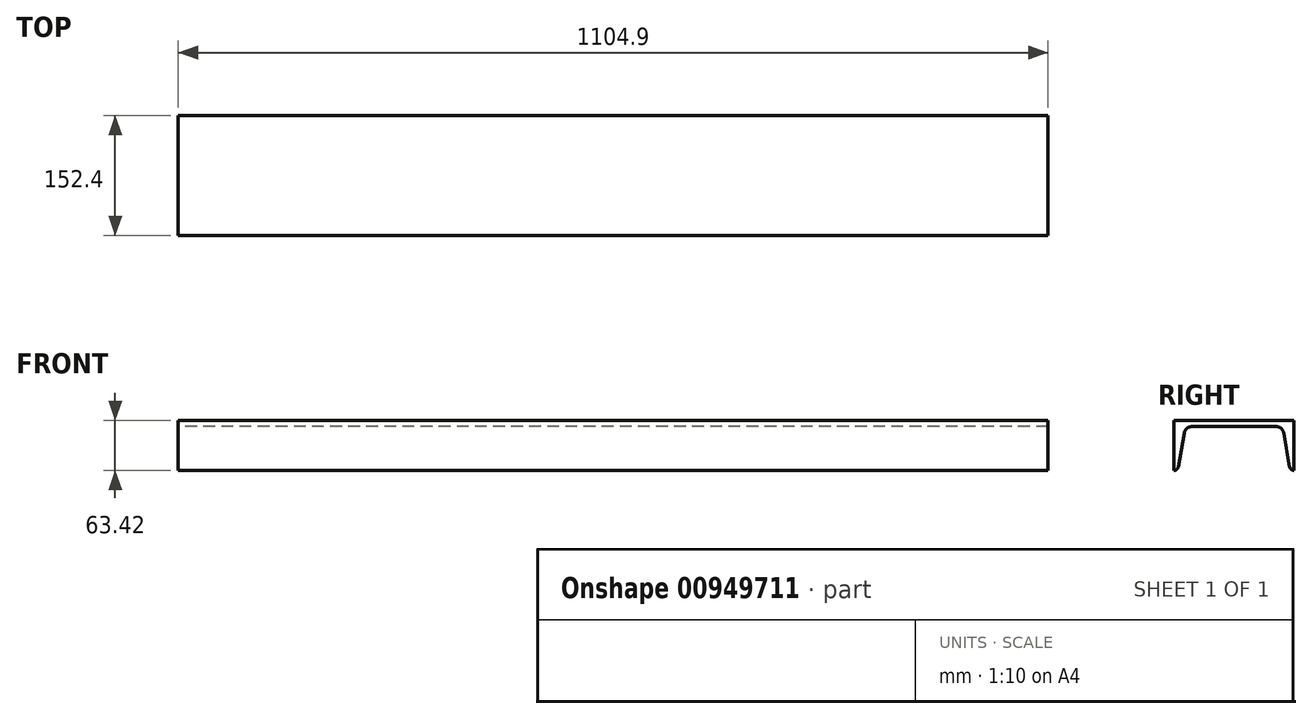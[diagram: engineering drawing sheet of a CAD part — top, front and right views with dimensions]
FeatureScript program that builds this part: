
annotation { "Feature Type Name" : "Feature", "Feature Type Description" : "" }
export const myFeature = defineFeature(function(context is Context, id is Id, definition is map)
    precondition{}
    {
        {
            var Q0;
            Q0=qCreatedBy(makeId("Right.planeOp"),FACE);
            var sketch = newSketch(context, id + "F0", { "sketchPlane" : qUnion([Q0])});
            skLineSegment(sketch, "E0", {"start": v(-76.2, 0) * mm, "end": v(76.2, 0) * mm});
            skLineSegment(sketch, "E1", {"start": v(76.2, 0) * mm, "end": v(76.2, -63.42) * mm});
            skLineSegment(sketch, "E2", {"start": v(-76.2, 0) * mm, "end": v(-76.2, -63.42) * mm});
            skLineSegment(sketch, "E3", {"start": v(-63.12, -15.57) * mm, "end": v(-70.65, -58.76) * mm});
            skLineSegment(sketch, "E4", {"start": v(63.12, -15.57) * mm, "end": v(70.65, -58.76) * mm});
            skLineSegment(sketch, "E5", {"start": v(-53.98, -7.87) * mm, "end": v(53.98, -7.87) * mm});
            skArc(sketch, "E6.filletArc", {"start": v(-76.2, -63.42) * mm, "mid": v(-72.57, -62.1) * mm, "end": v(-70.65, -58.76) * mm});
            skArc(sketch, "E7.filletArc", {"start": v(70.65, -58.76) * mm, "mid": v(72.57, -62.1) * mm, "end": v(76.2, -63.42) * mm});
            skArc(sketch, "E8.filletArc", {"start": v(-53.98, -7.87) * mm, "mid": v(-59.95, -10.05) * mm, "end": v(-63.12, -15.57) * mm});
            skArc(sketch, "E9.filletArc", {"start": v(63.12, -15.57) * mm, "mid": v(59.95, -10.05) * mm, "end": v(53.98, -7.87) * mm});
            skSolve(sketch);
        }
        {
            var Q0;
            Q0=qSketchRegion(id+"F0",true);
            extrude(context, id + "F1", {"entities" : qUnion([Q0]), "depth" : 1104.9 * mm, "offsetDistance" : 25.4 * mm});
        }
    });
